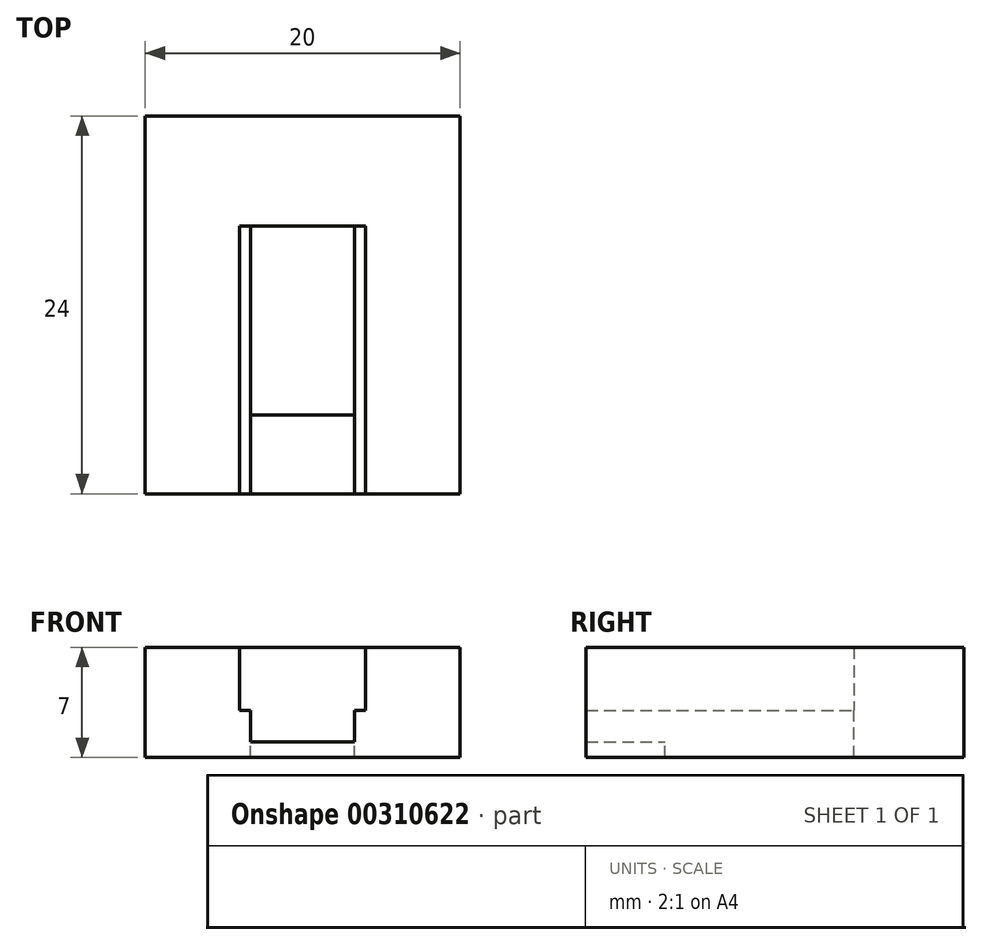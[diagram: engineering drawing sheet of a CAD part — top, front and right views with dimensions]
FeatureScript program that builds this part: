
annotation { "Feature Type Name" : "Feature", "Feature Type Description" : "" }
export const myFeature = defineFeature(function(context is Context, id is Id, definition is map)
    precondition{}
    {
        {
            var Q0;
            Q0=qCreatedBy(makeId("Front.planeOp"),FACE);
            var sketch = newSketch(context, id + "F0", { "sketchPlane" : qUnion([Q0])});
            skLineSegment(sketch, "E0.bottom", {"start": v(-10, 4) * mm, "end": v(10, 4) * mm});
            skLineSegment(sketch, "E0.top", {"start": v(-10, -3) * mm, "end": v(10, -3) * mm});
            skLineSegment(sketch, "E0.left", {"start": v(-10, 4) * mm, "end": v(-10, -3) * mm});
            skLineSegment(sketch, "E0.right", {"start": v(10, 4) * mm, "end": v(10, -3) * mm});
            skLineSegment(sketch, "E1.bottom", {"start": v(-4, 4) * mm, "end": v(4, 4) * mm});
            skLineSegment(sketch, "E1.top", {"start": v(-4, 0) * mm, "end": v(4, 0) * mm});
            skLineSegment(sketch, "E1.left", {"start": v(-4, 4) * mm, "end": v(-4, 0) * mm});
            skLineSegment(sketch, "E1.right", {"start": v(4, 4) * mm, "end": v(4, 0) * mm});
            skLineSegment(sketch, "E2.bottom", {"start": v(-4, 4) * mm, "end": v(-3.25, 4) * mm});
            skLineSegment(sketch, "E2.top", {"start": v(-4, 2) * mm, "end": v(-3.25, 2) * mm});
            skLineSegment(sketch, "E2.left", {"start": v(-4, 4) * mm, "end": v(-4, 2) * mm});
            skLineSegment(sketch, "E2.right", {"start": v(-3.25, 4) * mm, "end": v(-3.25, 2) * mm});
            skLineSegment(sketch, "E3.bottom", {"start": v(4, 4) * mm, "end": v(3.25, 4) * mm});
            skLineSegment(sketch, "E3.top", {"start": v(4, 2) * mm, "end": v(3.25, 2) * mm});
            skLineSegment(sketch, "E3.left", {"start": v(4, 4) * mm, "end": v(4, 2) * mm});
            skLineSegment(sketch, "E3.right", {"start": v(3.25, 4) * mm, "end": v(3.25, 2) * mm});
            skSolve(sketch);
        }
        {
            var Q0;
            Q0=makeQuery(id+"F0.imprint","IMPRINT",FACE,{"disambiguationData":[TD([[makeQuery(id+"F0.imprint","IMPRINT",EDGE,{"derivedFrom":sQuery(id+"F0.wireOp",EDGE,"E0.top")}),1.0]])]});
            var Q1;
            Q1=makeQuery(id+"F0.imprint","IMPRINT",FACE,{"disambiguationData":[TD([[makeQuery(id+"F0.imprint","IMPRINT",EDGE,{"derivedFrom":sQuery(id+"F0.wireOp",EDGE,"E2.bottom")}),-1.0]])]});
            var Q2;
            Q2=makeQuery(id+"F0.imprint","IMPRINT",FACE,{"disambiguationData":[TD([[makeQuery(id+"F0.imprint","IMPRINT",EDGE,{"derivedFrom":sQuery(id+"F0.wireOp",EDGE,"E3.bottom")}),1.0]])]});
            extrude(context, id + "F1", {"entities" : qUnion([Q0, Q1, Q2]), "endBound" : BoundingType.SYMMETRIC, "depth" : 24 * mm});
        }
        {
            var Q0;
            Q0=qCreatedBy(makeId("Front.planeOp"),FACE);
            var sketch = newSketch(context, id + "F2", { "sketchPlane" : qUnion([Q0])});
            skLineSegment(sketch, "E4.bottom", {"start": v(-3.31, 0) * mm, "end": v(3.31, 0) * mm});
            skLineSegment(sketch, "E4.top", {"start": v(-3.31, -2) * mm, "end": v(3.31, -2) * mm});
            skLineSegment(sketch, "E4.left", {"start": v(-3.31, 0) * mm, "end": v(-3.31, -2) * mm});
            skLineSegment(sketch, "E4.right", {"start": v(3.31, 0) * mm, "end": v(3.31, -2) * mm});
            skSolve(sketch);
        }
        {
            var Q0;
            Q0 = qSketchRegion(id + "F2", true);
            extrude(context, id + "F3", {"entities" : qUnion([Q0]), "operationType" : NewBodyOperationType.REMOVE, "depth" : 12 * mm});
        }
        {
            var Q0;
            Q0=makeQuery(id+"F2.imprint","IMPRINT",FACE,{"disambiguationData":[TD([[makeQuery(id+"F2.imprint","IMPRINT",EDGE,{"derivedFrom":sQuery(id+"F2.wireOp",EDGE,"E4.bottom")}),-1.0]])]});
            extrude(context, id + "F4", {"entities" : qUnion([Q0]), "operationType" : NewBodyOperationType.REMOVE, "oppositeDirection" : true, "depth" : 8 * mm});
        }
        {
            var Q0;
            Q0=qCreatedBy(makeId("Top.planeOp"),FACE);
            var sketch = newSketch(context, id + "F5", { "sketchPlane" : qUnion([Q0])});
            skLineSegment(sketch, "E5.bottom", {"start": v(-4, 12) * mm, "end": v(4, 12) * mm});
            skLineSegment(sketch, "E5.top", {"start": v(-4, 8) * mm, "end": v(4, 8) * mm});
            skLineSegment(sketch, "E5.left", {"start": v(-4, 12) * mm, "end": v(-4, 8) * mm});
            skLineSegment(sketch, "E5.right", {"start": v(4, 12) * mm, "end": v(4, 8) * mm});
            skSolve(sketch);
        }
        {
            var Q0;
            Q0=makeQuery(id+"F5.imprint","IMPRINT",FACE,{"disambiguationData":[TD([[makeQuery(id+"F5.imprint","IMPRINT",EDGE,{"derivedFrom":sQuery(id+"F5.wireOp",EDGE,"E5.bottom")}),-1.0]])]});
            extrude(context, id + "F6", {"entities" : qUnion([Q0]), "operationType" : NewBodyOperationType.ADD, "depth" : 4 * mm});
        }
        {
            var Q0;
            Q0=qCreatedBy(makeId("Top.planeOp"),FACE);
            var sketch = newSketch(context, id + "F7", { "sketchPlane" : qUnion([Q0])});
            skLineSegment(sketch, "E6.bottom", {"start": v(-3.31, 5) * mm, "end": v(3.3, 5) * mm});
            skLineSegment(sketch, "E6.top", {"start": v(-3.3, -7) * mm, "end": v(3.31, -7) * mm});
            skLineSegment(sketch, "E6.left", {"start": v(-3.31, 5) * mm, "end": v(-3.3, -7) * mm});
            skLineSegment(sketch, "E6.right", {"start": v(3.3, 5) * mm, "end": v(3.31, -7) * mm});
            skSolve(sketch);
        }
        {
            var Q0;
            Q0=makeQuery(id+"F7.imprint","IMPRINT",FACE,{"disambiguationData":[TD([[makeQuery(id+"F7.imprint","IMPRINT",EDGE,{"derivedFrom":sQuery(id+"F7.wireOp",EDGE,"E6.bottom")}),-1.0]])]});
            extrude(context, id + "F8", {"entities" : qUnion([Q0]), "operationType" : NewBodyOperationType.REMOVE, "oppositeDirection" : true, "depth" : 3 * mm});
        }
        {
            var Q0;
            Q0=makeQuery(id+"F6.boolean.opBoolean","MERGE",FACE,{"derivedFrom":[makeQuery(id+"F4.boolean.opBoolean","COPY",FACE,{"derivedFrom":makeQuery(id+"F4.opExtrude","CAP_FACE",FACE,{"disambiguationData":[OSD([sQuery(id+"F2.wireOp",EDGE,"E4.bottom"),sQuery(id+"F2.wireOp",EDGE,"E4.top"),sQuery(id+"F2.wireOp",EDGE,"E4.left"),sQuery(id+"F2.wireOp",EDGE,"E4.right")])],"isStart":false})}),makeQuery(id+"F6.opExtrude","SWEPT_FACE",FACE,{"disambiguationData":[OSD([sQuery(id+"F5.wireOp",EDGE,"E5.top")])]})]});
            extrude(context, id + "F9", {"entities" : qUnion([Q0]), "operationType" : NewBodyOperationType.ADD, "depth" : 3 * mm});
        }
    });
